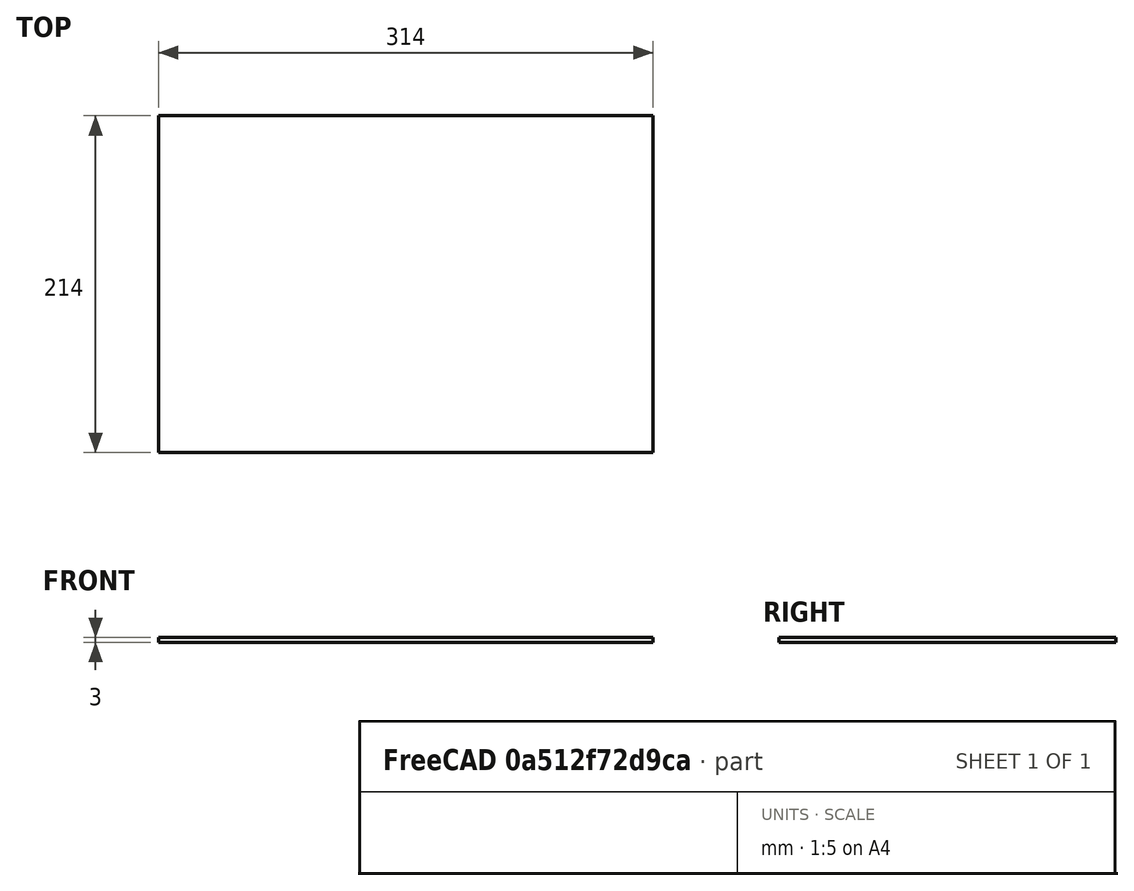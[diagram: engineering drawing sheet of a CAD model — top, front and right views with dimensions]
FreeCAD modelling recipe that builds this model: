
FCSTD DOCUMENT  (FreeCAD 0.16R4945 (Git))
Label: MK3-300x200b
License: CreativeCommons Attribution-ShareAlike
LicenseURL: http://creativecommons.org/licenses/by-sa/4.0/
objects: Sketcher::SketchObject×3, PartDesign::Pad×1
note: 5 computed .brp shape members not serialized (recipe doc carries the construction recipe); baked Part::Feature solids carry a one-line shape summary decoded from their .brp

FEATURE [Sketcher::SketchObject] Sketch001  label="Sketch003"
  Placement = pos=(110.544,322.172,403.913) rot=(0,0,-1;1.5708rad)
  sketch-geometry (4):
    g0: LineSegment StartX=-214 StartY=314 StartZ=0 EndX=0 EndY=314 EndZ=0
    g1: LineSegment StartX=0 StartY=314 StartZ=0 EndX=0 EndY=0 EndZ=0
    g2: LineSegment StartX=0 StartY=0 StartZ=0 EndX=-214 EndY=0 EndZ=0
    g3: LineSegment StartX=-214 StartY=0 StartZ=0 EndX=-214 EndY=314 EndZ=0
  constraints (11):
    c: Coincident(g0,g1)
    c: Coincident(g1,g2)
    c: Coincident(g2,g3)
    c: Coincident(g3,g0)
    c: Horizontal(g0)
    c: Horizontal(g2)
    c: Vertical(g1)
    c: Vertical(g3)
    c: Distance(g2) = 214
    c: Distance(g1) = 314
    c: Coincident(g1,g-1)
FEATURE [PartDesign::Pad] Pad
  Length = 3
  Length2 = 100
  Placement = pos=(110.544,322.172,403.913) rot=(0,0,-1;1.5708rad)
  Sketch = -> Sketch001
  Type = 0
FEATURE [Sketcher::SketchObject] Sketch  label="Sketch001"
  ExternalGeometry = -> [Pad]
  Placement = pos=(110.544,322.172,406.913) rot=(0,0,-1;1.5708rad)
  Support = -> Pad [Face6]
  sketch-geometry (25):
    g0: LineSegment StartX=-210 StartY=132.5 StartZ=0 EndX=-206 EndY=132.5 EndZ=0
    g1: LineSegment StartX=-206 StartY=132.5 StartZ=0 EndX=-206 EndY=147.5 EndZ=0
    g2: LineSegment StartX=-206 StartY=147.5 StartZ=0 EndX=-210 EndY=147.5 EndZ=0
    g3: LineSegment StartX=-210 StartY=147.5 StartZ=0 EndX=-210 EndY=132.5 EndZ=0
    g4: LineSegment StartX=-210 StartY=172.5 StartZ=0 EndX=-206 EndY=172.5 EndZ=0
    g5: LineSegment StartX=-206 StartY=172.5 StartZ=0 EndX=-206 EndY=187.5 EndZ=0
    g6: LineSegment StartX=-206 StartY=187.5 StartZ=0 EndX=-210 EndY=187.5 EndZ=0
    g7: LineSegment StartX=-210 StartY=187.5 StartZ=0 EndX=-210 EndY=172.5 EndZ=0
    g8: LineSegment StartX=-210 StartY=190.5 StartZ=0 EndX=-206 EndY=190.5 EndZ=0
    g9: LineSegment StartX=-206 StartY=190.5 StartZ=0 EndX=-206 EndY=205.5 EndZ=0
    g10: LineSegment StartX=-206 StartY=205.5 StartZ=0 EndX=-210 EndY=205.5 EndZ=0
    g11: LineSegment StartX=-210 StartY=205.5 StartZ=0 EndX=-210 EndY=190.5 EndZ=0
    g12: LineSegment [constr] StartX=0 StartY=157 StartZ=0 EndX=-214 EndY=157 EndZ=0
    g13: LineSegment StartX=-211 StartY=164.5 StartZ=0 EndX=-209 EndY=164.5 EndZ=0
    g14: LineSegment StartX=-209 StartY=164.5 StartZ=0 EndX=-209 EndY=160.5 EndZ=0
    g15: LineSegment StartX=-209 StartY=160.5 StartZ=0 EndX=-211 EndY=160.5 EndZ=0
    g16: LineSegment StartX=-211 StartY=160.5 StartZ=0 EndX=-211 EndY=164.5 EndZ=0
    g17: LineSegment StartX=-208 StartY=164.5 StartZ=0 EndX=-206 EndY=164.5 EndZ=0
    g18: LineSegment StartX=-206 StartY=164.5 StartZ=0 EndX=-206 EndY=160.5 EndZ=0
    g19: LineSegment StartX=-206 StartY=160.5 StartZ=0 EndX=-208 EndY=160.5 EndZ=0
    g20: LineSegment StartX=-208 StartY=160.5 StartZ=0 EndX=-208 EndY=164.5 EndZ=0
    g21: LineSegment StartX=-208.841 StartY=164.835 StartZ=0 EndX=-206.841 EndY=164.835 EndZ=0
    g22: LineSegment StartX=-206.841 StartY=164.835 StartZ=0 EndX=-206.841 EndY=168.835 EndZ=0
    g23: LineSegment StartX=-206.841 StartY=168.835 StartZ=0 EndX=-208.841 EndY=168.835 EndZ=0
    g24: LineSegment StartX=-208.841 StartY=168.835 StartZ=0 EndX=-208.841 EndY=164.835 EndZ=0
  constraints (74):
    c: Coincident(g0,g1)
    c: Coincident(g1,g2)
    c: Coincident(g2,g3)
    c: Coincident(g3,g0)
    c: Horizontal(g0)
    c: Horizontal(g2)
    c: Vertical(g1)
    c: Vertical(g3)
    c: Coincident(g4,g5)
    c: Coincident(g5,g6)
    c: Coincident(g6,g7)
    c: Coincident(g7,g4)
    c: Horizontal(g4)
    c: Horizontal(g6)
    c: Vertical(g5)
    c: Vertical(g7)
    c: Coincident(g8,g9)
    c: Coincident(g9,g10)
    c: Coincident(g10,g11)
    c: Coincident(g11,g8)
    c: Horizontal(g8)
    c: Horizontal(g10)
    c: Vertical(g9)
    c: Vertical(g11)
    c: Distance(g1) = 15
    c: Distance(g2) = 4
    c: Distance(g5) = 15
    c: Distance(g9) = 15
    c: Distance(g6) = 4
    c: Distance(g10) = 4
    c: Horizontal(g12)
    c: PointOnObject(g12,g-2)
    c: DistanceY(g12,g8) = 33.5
    c: Coincident(g13,g14)
    c: Coincident(g14,g15)
    c: Coincident(g15,g16)
    c: Coincident(g16,g13)
    c: Horizontal(g13)
    c: Horizontal(g15)
    c: Vertical(g14)
    c: Vertical(g16)
    c: Coincident(g17,g18)
    c: Coincident(g18,g19)
    c: Coincident(g19,g20)
    c: Coincident(g20,g17)
    c: Horizontal(g17)
    c: Horizontal(g19)
    c: Vertical(g18)
    c: Vertical(g20)
    c: Coincident(g21,g22)
    c: Coincident(g22,g23)
    c: Coincident(g23,g24)
    c: Coincident(g24,g21)
    c: Horizontal(g21)
    c: Horizontal(g23)
    c: Vertical(g22)
    c: Vertical(g24)
    c: Distance(g23) = 2
    c: Distance(g13) = 2
    c: Distance(g17) = 2
    c: Distance(g14) = 4
    c: Distance(g18) = 4
    c: Distance(g22) = 4
    c: DistanceX(g17,g13) = -1
    c: PointOnObject(g12,g-3)
    c: Symmetric(g-3,g-3,g12)
    c: DistanceX(g2,g12) = -4
    c: DistanceY(g2,g12) = 9.5
    c: DistanceY(g12,g15) = 3.5
    c: DistanceY(g12,g19) = 3.5
    c: DistanceY(g12,g4) = 15.5
    c: DistanceX(g12,g4) = 4
    c: DistanceX(g12,g8) = 4
    c: DistanceX(g12,g15) = 3
FEATURE [Sketcher::SketchObject] Sketch002
  Placement = pos=(110.544,322.172,406.913) rot=(0,0,-1;1.5708rad)
  sketch-geometry (21):
    g0: Circle CenterX=6 CenterY=89.9816 CenterZ=0 NormalX=0 NormalY=0 NormalZ=1 Radius=1.5
    g1: Circle CenterX=3 CenterY=107.505 CenterZ=0 NormalX=0 NormalY=0 NormalZ=1 Radius=1.5
    g2: Circle CenterX=4.03082 CenterY=112.011 CenterZ=0 NormalX=0 NormalY=0 NormalZ=1 Radius=0.785821
    g3: Circle CenterX=4.01639 CenterY=113.975 CenterZ=0 NormalX=0 NormalY=0 NormalZ=1 Radius=0.76265
    g4: Circle CenterX=7.02069 CenterY=112.011 CenterZ=0 NormalX=0 NormalY=0 NormalZ=1 Radius=0.715221
    g5: Circle CenterX=7.02069 CenterY=114.004 CenterZ=0 NormalX=0 NormalY=0 NormalZ=1 Radius=0.716106
    g6: Circle CenterX=6.02408 CenterY=115.997 CenterZ=0 NormalX=0 NormalY=0 NormalZ=1 Radius=0.729944
    g7: Circle CenterX=3.59863 CenterY=118.019 CenterZ=0 NormalX=0 NormalY=0 NormalZ=1 Radius=0.598632
    g8: Circle CenterX=6 CenterY=131.026 CenterZ=0 NormalX=0 NormalY=0 NormalZ=1 Radius=1.5
    g9: Circle CenterX=6 CenterY=148.037 CenterZ=0 NormalX=0 NormalY=0 NormalZ=1 Radius=1.5
    g10: Circle CenterX=3 CenterY=365.224 CenterZ=0 NormalX=0 NormalY=0 NormalZ=1 Radius=1.5
    g11: Circle CenterX=3 CenterY=206.724 CenterZ=0 NormalX=0 NormalY=0 NormalZ=1 Radius=1.5
    g12: Circle CenterX=211 CenterY=210.724 CenterZ=0 NormalX=0 NormalY=0 NormalZ=1 Radius=1.5
    g13: Circle CenterX=211 CenterY=365.224 CenterZ=0 NormalX=0 NormalY=0 NormalZ=1 Radius=1.5
    g14: ArcOfCircle CenterX=113.5 CenterY=350.994 CenterZ=0 NormalX=0 NormalY=0 NormalZ=1 Radius=1.5 StartAngle=3.14159 EndAngle=6.28319
    g15: LineSegment StartX=112 StartY=356.994 StartZ=0 EndX=112 EndY=350.994 EndZ=0
    g16: LineSegment StartX=115 StartY=356.994 StartZ=0 EndX=115 EndY=350.994 EndZ=0
    g17: LineSegment [constr] StartX=6 StartY=89.9816 StartZ=0 EndX=6 EndY=148.037 EndZ=0
    g18: LineSegment [constr] StartX=3 StartY=206.724 StartZ=0 EndX=3 EndY=365.224 EndZ=0
    g19: LineSegment [constr] StartX=211 StartY=210.724 StartZ=0 EndX=211 EndY=365.224 EndZ=0
    g20: LineSegment StartX=115 StartY=356.994 StartZ=0 EndX=112 EndY=356.994 EndZ=0
  constraints (31):
    c: Tangent(g15,g14) = -1.5708
    c: Tangent(g16,g14) = 1.5708
    c: Vertical(g15)
    c: Radius(g0) = 1.5
    c: DistanceX(g-1,g0) = 6
    c: Coincident(g17,g0)
    c: Coincident(g17,g9)
    c: Vertical(g17)
    c: PointOnObject(g8,g17)
    c: Radius(g8) = 1.5
    c: Radius(g9) = 1.5
    c: DistanceX(g-1,g1) = 3
    c: Radius(g1) = 1.5
    c: Radius(g11) = 1.5
    c: Radius(g10) = 1.5
    c: Coincident(g18,g11)
    c: Coincident(g18,g10)
    c: Vertical(g18)
    c: Tangent(g18,g7)
    c: PointOnObject(g1,g18)
    c: Radius(g12) = 1.5
    c: Radius(g13) = 1.5
    c: Coincident(g19,g12)
    c: Coincident(g19,g13)
    c: Vertical(g19)
    c: Radius(g14) = 1.5
    c: Coincident(g20,g15)
    c: Horizontal(g20)
    c: Coincident(g16,g20)
    c: Distance(g16) = 6
    c: Vertical(g16)
